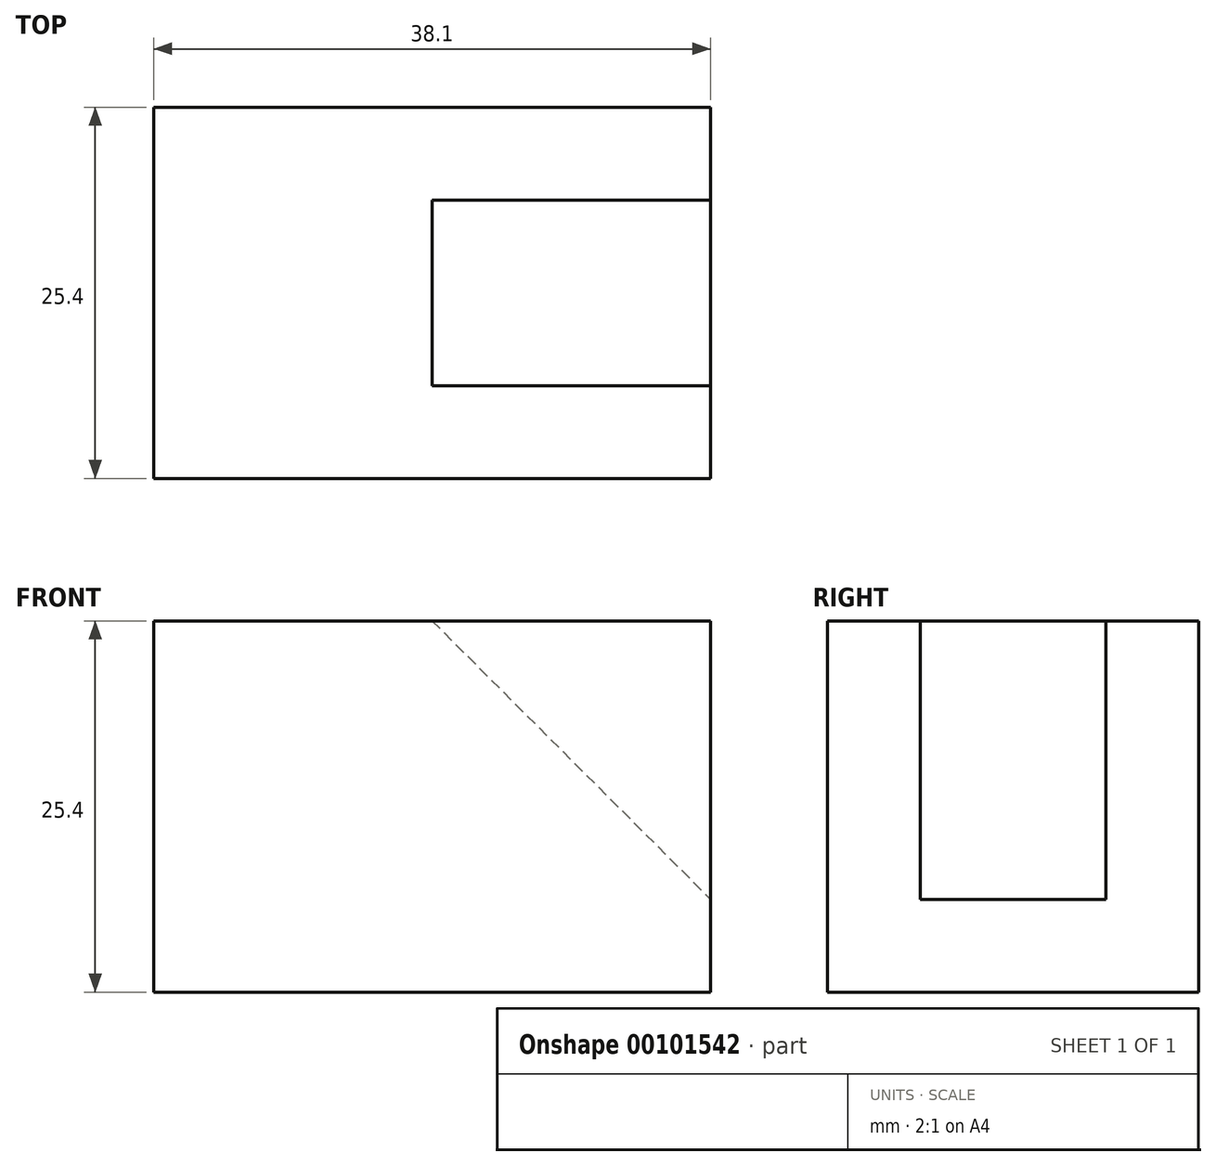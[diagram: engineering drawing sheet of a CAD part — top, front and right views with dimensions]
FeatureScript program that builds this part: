
annotation { "Feature Type Name" : "Feature", "Feature Type Description" : "" }
export const myFeature = defineFeature(function(context is Context, id is Id, definition is map)
    precondition{}
    {
        {
            var Q0;
            Q0=qCreatedBy(makeId("Front.planeOp"),FACE);
            var sketch = newSketch(context, id + "F0", { "sketchPlane" : qUnion([Q0])});
            skLineSegment(sketch, "E0", {"start": v(0, 0) * mm, "end": v(38.1, 0) * mm});
            skLineSegment(sketch, "E1", {"start": v(38.1, 0) * mm, "end": v(38.1, 25.4) * mm});
            skLineSegment(sketch, "E2", {"start": v(38.1, 25.4) * mm, "end": v(0, 25.4) * mm});
            skLineSegment(sketch, "E3", {"start": v(0, 25.4) * mm, "end": v(0, 0) * mm});
            skLineSegment(sketch, "E4", {"start": v(19.05, 25.4) * mm, "end": v(38.1, 6.35) * mm});
            skSolve(sketch);
        }
        {
            var Q0;
            {var subQ4=sQuery(id+"F0.wireOp",EDGE,"E0");Q0=makeQuery(id+"F0.imprint","IMPRINT",FACE,{"disambiguationData":[TD([[makeQuery(id+"F0.imprint","IMPRINT",EDGE,{"derivedFrom":subQ4}),1.0]])]});}
            extrude(context, id + "F1", {"entities" : qUnion([Q0]), "endBound" : BoundingType.SYMMETRIC, "depth" : 25.4 * mm});
        }
        {
            var Q0;
            {var subQ3=sQuery(id+"F0.wireOp",EDGE,"E4");Q0=makeQuery(id+"F0.imprint","IMPRINT",FACE,{"disambiguationData":[TD([[makeQuery(id+"F0.imprint","IMPRINT",EDGE,{"derivedFrom":subQ3}),1.0]])]});}
            extrude(context, id + "F2", {"entities" : qUnion([Q0]), "operationType" : NewBodyOperationType.ADD, "depth" : 12.7 * mm, "hasSecondDirection" : true, "secondDirectionOppositeDirection" : false, "secondDirectionDepth" : 6.35 * mm});
        }
        {
            var Q0;
            {var subQ3=sQuery(id+"F0.wireOp",EDGE,"E4");Q0=makeQuery(id+"F0.imprint","IMPRINT",FACE,{"disambiguationData":[TD([[makeQuery(id+"F0.imprint","IMPRINT",EDGE,{"derivedFrom":subQ3}),1.0]])]});}
            extrude(context, id + "F3", {"entities" : qUnion([Q0]), "operationType" : NewBodyOperationType.ADD, "oppositeDirection" : true, "depth" : 12.7 * mm, "hasSecondDirection" : true, "secondDirectionOppositeDirection" : true, "secondDirectionDepth" : 6.35 * mm});
        }
    });
